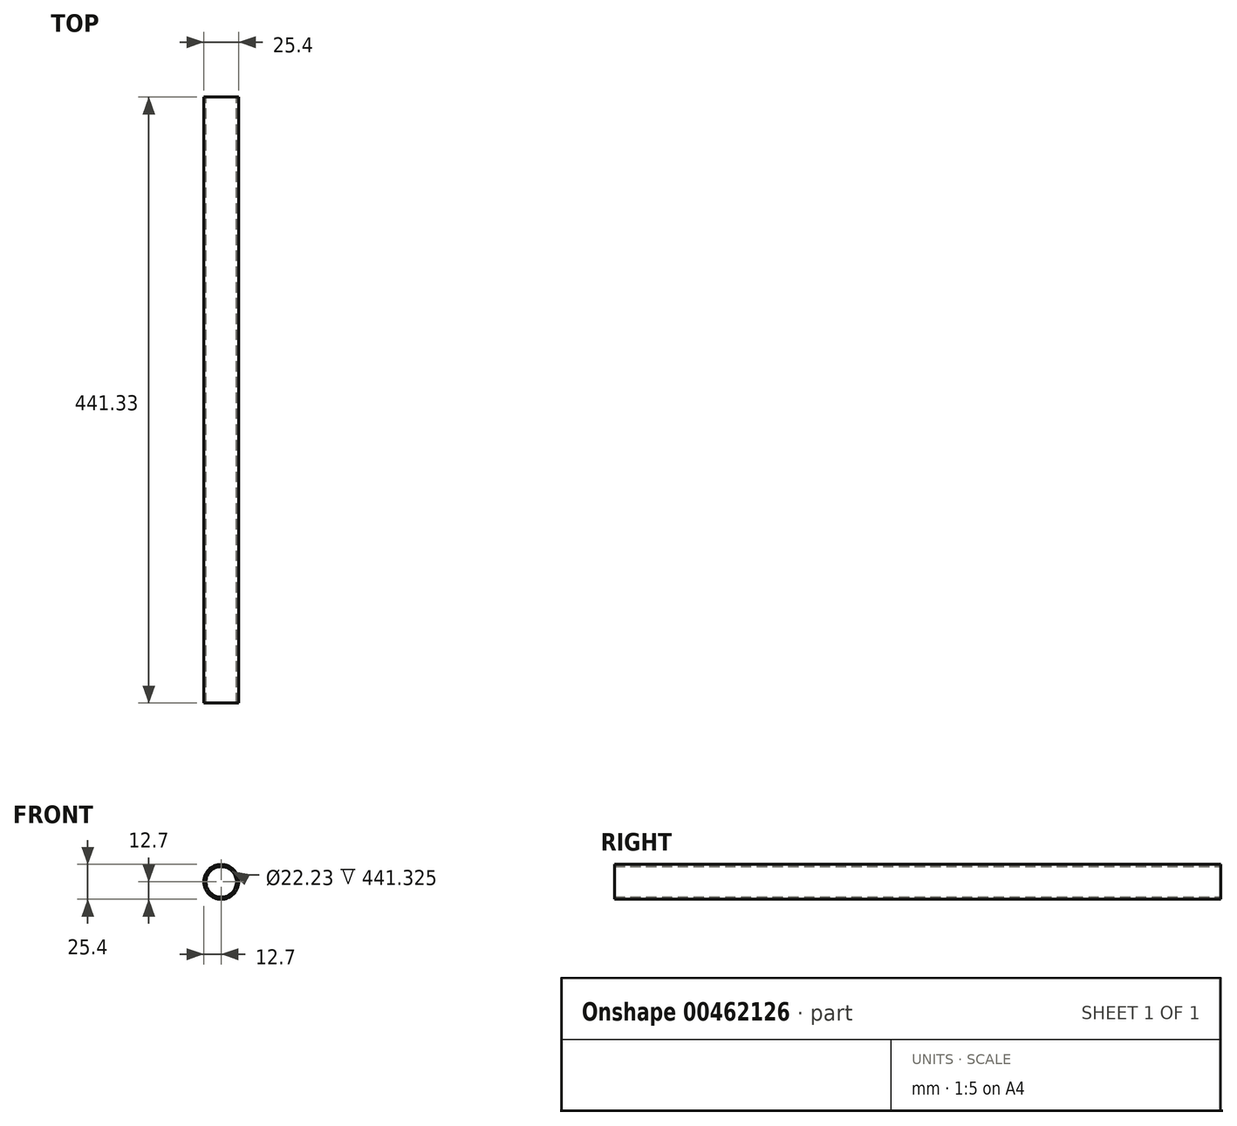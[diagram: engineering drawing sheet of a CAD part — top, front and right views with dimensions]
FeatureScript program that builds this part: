
annotation { "Feature Type Name" : "Feature", "Feature Type Description" : "" }
export const myFeature = defineFeature(function(context is Context, id is Id, definition is map)
    precondition{}
    {
        {
            var Q0;
            Q0=qCreatedBy(makeId("Front.planeOp"),FACE);
            var sketch = newSketch(context, id + "F0", { "sketchPlane" : qUnion([Q0])});
            skCircle(sketch, "E0", {"center": v(0, 0) * mm, "radius": 12.7 * mm});
            skCircle(sketch, "E1", {"center": v(0, 0) * mm, "radius": 11.11 * mm});
            skSolve(sketch);
        }
        {
            var Q0;
            Q0 = qSketchRegion(id + "F0", true);
            extrude(context, id + "F1", {"entities" : qUnion([Q0]), "depth" : 441.32 * mm});
        }
    });
